# Revit family: IS_StradaII_T3644_BIM_GB
name_source: partatom
category: Plumbing Fixtures
revit_build: Autodesk Revit 2017 (Build: 20160225_1515(x64)
units: mm (PartAtom-declared; Revit-internal decimal feet)

## family parameters
Always vertical = No
Cut with Voids When Loaded = No
OmniClass Number = 23.45.05.14.14
OmniClass Title = Sinks/Lavatories
Part Type = Normal
Room Calculation Point = No
Round Connector Dimension = Use Diameter
Shared = No
Work Plane-Based = No

## types (2) — shared parameters
Accessories = http://www.idealstandard.de
AssetType = Fixed
BIMObjectName = ISI_IdealStandard_Washhandbasin_StradaII_T3644
BOSUseNativeGeometries = 1
Brand = Ideal Standard
Brand url = http://www.idealstandard.de
Category = Sanitary
Color = WHITE
ConnectionType = Plumbing
CurrencyUnit = €
CurrentRevision = 1
Date of publishing = 43172
DurationUnit = year
Edition number = 1
Finish = WHITE
GrossWeight = 17
IfcExportAs = IfcSanitaryTerminalType
IfcExportType = WASHHANDBASIN
Installation instructions = http://www.idealstandard.de
InstallationDate = 1900-12-31T23:59:59
InstallationInstructions = http://www.idealstandard.de
MainColor = WHITE
Manufacturer = http://www.idealstandard.de
Manufacturer name = Ideal Standard
ManufacturerURL = http://www.idealstandard.de
Material = Fire clay
Material main = Ceramics
NBS Reference Code = 45-35-70/365
NBS Reference Description = Pedestal Wash basins
Name = ISI_IdealStandard_Washhandbasin_StradaII_T3644
NettWeight = 15
Nominal height = 130
Nominal width = 600
NominalDepth = 428 mm  [stored 1.4042 ft]
NominalHeight = 178 mm
NominalLength = 428 mm  [stored 1.4042 ft]
NominalWidth = 600 mm  [stored 1.9685 ft]
Product Guid = 3c610142-fe95-467b-853b-b3003161e490
Product SKU = T3644
Product data url = https://bimobject.com
Product family = Sanitary
Product group = Washbasins
Product url = http://www.idealstandard.de
ProductInformation = http://www.idealstandard.de
QR code = http://bimobject.com
ReplacementCost = 0
Shape = Sculptured
Size = 178 x 428 x 600mm
Space = Internal
SpareParts = http://www.idealstandard.de
Technical description = http://www.idealstandard.de
URL = http://www.idealstandard.de
Uniclass 2.0 Code = Pr_40_20_96_63
Uniclass 2.0 Description = Pedestal Wash basins
Uniclass 2015 Code = Pr_40_20_96_63
Uniclass 2015 Name = Pedestal Wash basins
Uniclass2015Code = Pr_40_20_96_63
Uniclass2015Title = Pedestal Wash basins
Uniclass2015Version = Products v1.1
Version = 1
VolumeUnits = Litre
WarrantyDurationUnit = year
WashHandBasinMounting = Pedestal
WashHandBasinType = Handrinse
Weight Net (Kg) = 15
zero-valued in all types: Cost, DrainSize

## per-type parameters (varying)
| type | BarCode | Description | EAN code | Features | Model | ModelNumber | ModelReference | Product name |
| T364401 - STRADA II BASIN 60 WHITE 1TH GRINDED | 8014140450337 | STRADA II BASIN 60 WHITE 1TH GRINDED | https://8014140450337 | BASIN 60 WHITE 1TH GRINDED | T364401 | T364401 | STRADA II BASIN 60 WHITE 1TH GRINDED | STRADA II BASIN 60 WHITE 1TH GRINDED |
| T3644MA - STRADA II BASIN 60 WHT IP 1TH GRINDED | 8014140450344 | STRADA II BASIN 60 WHT IP 1TH GRINDED | https://8014140450344 | BASIN 60 WHT IP 1TH GRINDED | T3644MA | T3644MA | STRADA II BASIN 60 WHT IP 1TH GRINDED | STRADA II BASIN 60 WHT IP 1TH GRINDED |

note: [stored X ft] marks values corroborated as IEEE doubles in the binary element streams (Revit-internal decimal feet)

## geometry (parser evidence)
native form markers: Sweep x1
no freeform markers — native parametric forms only
